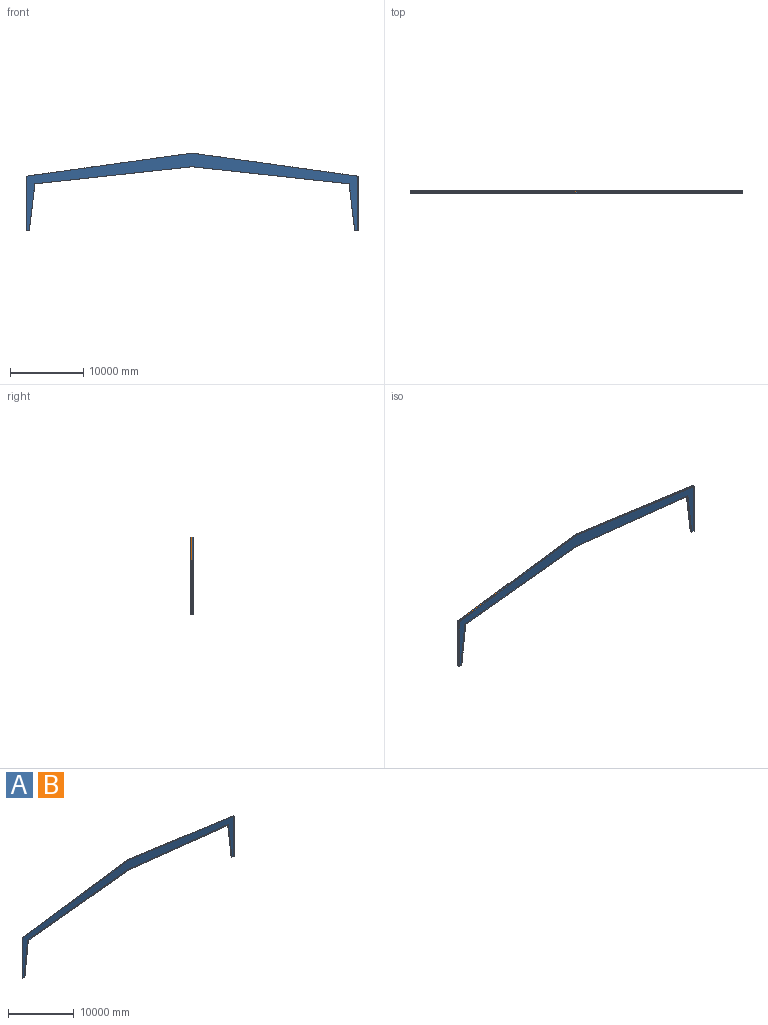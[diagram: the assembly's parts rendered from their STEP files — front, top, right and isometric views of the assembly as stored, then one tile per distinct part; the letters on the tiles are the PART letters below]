
ASSEMBLY  parts=2 mates=1
PART A: 23 faces, bbox 45415.2x152.4x10641.1 mm
  f0: plane 45415.2x10641.14mm, normal (0,-1,0), area 1496843.4mm2, adj f1,f2,f3,f4,f5,f6,f7,f8
  f1: plane 6425.73x762mm, normal (-0.99,0,-0.12), area 986143.4mm2, adj f0,f2,f10,f11
  f2: plane 457.2x152.4mm, normal (0,0,-1), area 69677.3mm2, adj f0,f1,f3,f11
  f3: plane 7487.3x152.4mm, normal (1,0,0), area 1141065.1mm2, adj f0,f2,f4,f11
  f4: plane 22707.6x3153.83mm, normal (0.14,0,0.99), area 3493856.9mm2, adj f0,f3,f5,f11
  f5: plane 22707.6x3153.83mm, normal (-0.14,0,0.99), area 3493856.9mm2, adj f0,f4,f6,f11
  f6: plane 7487.3x152.4mm, normal (-1,0,0), area 1141065.1mm2, adj f0,f5,f7,f11
  f7: plane 457.2x152.4mm, normal (0,0,-1), area 69677.3mm2, adj f0,f6,f8,f11
  f8: plane 6425.73x762mm, normal (0.99,0,-0.12), area 986143.4mm2, adj f0,f7,f9,f11
  f9: plane 21488.4x2337.27mm, normal (0.11,0,-0.99), area 3294146.9mm2, adj f0,f8,f10,f11
  f10: plane 21488.4x2337.27mm, normal (-0.11,0,-0.99), area 3294146.9mm2, adj f0,f1,f9,f11
  f11: plane 45415.2x10641.14mm, normal (0,1,0), area 80375383mm2, adj f1,f2,f3,f4,f5,f6,f7,f8
  f12: plane 6424.57x761.86mm, normal (0.99,0,0.12), area 903800.6mm2, adj f0,f13,f21,f22
  f13: plane 433.22x139.7mm, normal (0,0,1), area 60520.4mm2, adj f0,f12,f14,f22
  f14: plane 7463.55x139.7mm, normal (-1,0,0), area 1042657.3mm2, adj f0,f13,f15,f22
  f15: plane 22694.9x3152.07mm, normal (-0.14,0,-0.99), area 3200910.9mm2, adj f0,f14,f16,f22
  f16: plane 22694.9x3152.07mm, normal (0.14,0,-0.99), area 3200910.9mm2, adj f0,f15,f17,f22
  f17: plane 7463.55x139.7mm, normal (1,0,0), area 1042657.3mm2, adj f0,f16,f18,f22
  f18: plane 433.22x139.7mm, normal (0,0,1), area 60520.4mm2, adj f0,f17,f19,f22
  f19: plane 6424.57x761.86mm, normal (-0.99,0,0.12), area 903800.6mm2, adj f0,f18,f20,f22
  f20: plane 21499.82x2338.51mm, normal (-0.11,0,0.99), area 3021239.6mm2, adj f0,f19,f21,f22
  f21: plane 21499.82x2338.51mm, normal (0.11,0,0.99), area 3021239.6mm2, adj f0,f12,f20,f22
  f22: plane 45389.8x10615.62mm, normal (0,-1,0), area 78878539.6mm2, adj f12,f13,f14,f15,f16,f17,f18,f19
PART B: same geometry as A
PLACE A t=(-1905.74,-8663.54,-5425.95)mm
PLACE B rot(axis=(0,0,1),180deg) t=(-1905.74,-23801.94,-5425.95)mm
MATE fastened A.f11 <-> B.f11  axis (0,1,0) through (-1905.74,-16232.74,5215.18)mm
